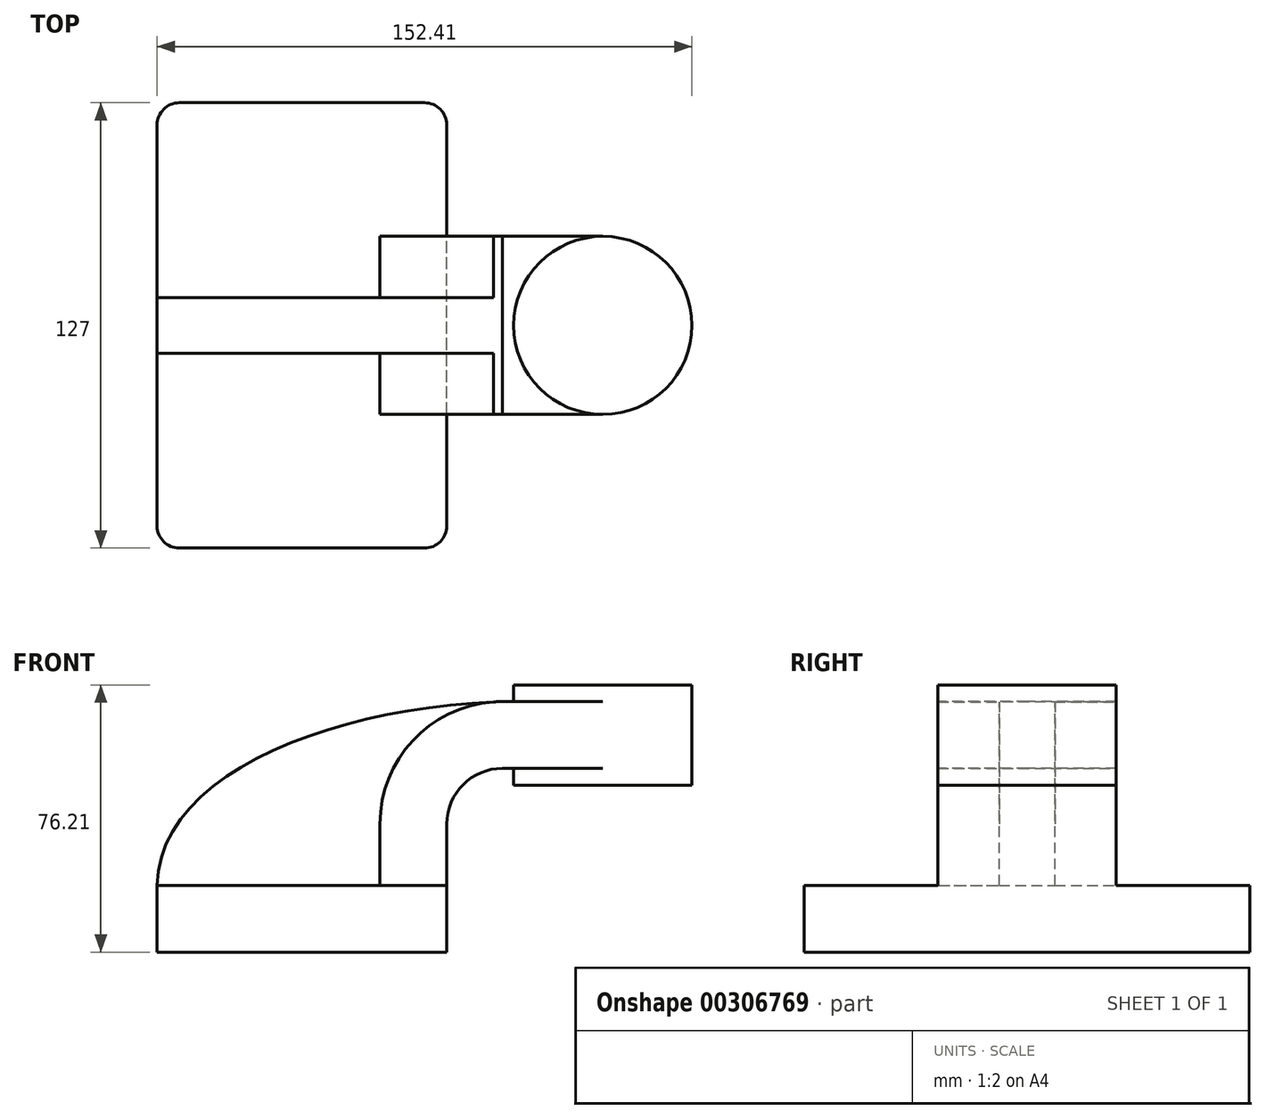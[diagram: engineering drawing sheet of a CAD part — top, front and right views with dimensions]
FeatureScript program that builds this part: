
annotation { "Feature Type Name" : "Feature", "Feature Type Description" : "" }
export const myFeature = defineFeature(function(context is Context, id is Id, definition is map)
    precondition{}
    {
        {
            var Q0;
            Q0=qCreatedBy(makeId("Front.planeOp"),FACE);
            var sketch = newSketch(context, id + "F0", { "sketchPlane" : qUnion([Q0])});
            skLineSegment(sketch, "E0.bottom", {"start": v(41.28, -9.52) * mm, "end": v(-41.28, -9.53) * mm});
            skLineSegment(sketch, "E0.top", {"start": v(41.27, 9.53) * mm, "end": v(-41.28, 9.53) * mm});
            skLineSegment(sketch, "E0.left", {"start": v(41.28, -9.52) * mm, "end": v(41.28, 9.53) * mm});
            skLineSegment(sketch, "E0.right", {"start": v(-41.28, -9.53) * mm, "end": v(-41.28, 9.53) * mm});
            skPoint(sketch, "E0.middle", {"position": v(0, 0) * mm});
            skLineSegment(sketch, "E1.bottom", {"start": v(111.12, 38.1) * mm, "end": v(60.33, 38.1) * mm});
            skLineSegment(sketch, "E1.top", {"start": v(111.12, 66.68) * mm, "end": v(60.33, 66.68) * mm});
            skLineSegment(sketch, "E1.left", {"start": v(111.12, 38.1) * mm, "end": v(111.12, 66.68) * mm});
            skLineSegment(sketch, "E1.right", {"start": v(60.33, 38.1) * mm, "end": v(60.33, 66.68) * mm});
            skPoint(sketch, "E1.middle", {"position": v(85.72, 52.39) * mm});
            skLineSegment(sketch, "E2", {"start": v(41.27, 9.53) * mm, "end": v(41.27, 27) * mm});
            skArc(sketch, "E3", {"start": v(41.27, 27) * mm, "mid": v(45.92, 38.23) * mm, "end": v(57.15, 42.88) * mm});
            skLineSegment(sketch, "E4", {"start": v(57.15, 42.88) * mm, "end": v(85.72, 42.88) * mm});
            skLineSegment(sketch, "E5", {"start": v(85.72, 42.88) * mm, "end": v(85.72, 42.88) * mm});
            skLineSegment(sketch, "E6.0", {"start": v(57.15, 61.93) * mm, "end": v(85.72, 61.93) * mm});
            skArc(sketch, "E6.1", {"start": v(22.23, 27) * mm, "mid": v(32.45, 51.7) * mm, "end": v(57.15, 61.93) * mm});
            skLineSegment(sketch, "E6.2", {"start": v(22.22, 9.53) * mm, "end": v(22.22, 27) * mm});
            skLineSegment(sketch, "E7", {"start": v(85.72, 38.1) * mm, "end": v(85.72, 66.68) * mm});
            skFitSpline(sketch, "E8", {"points": [v(-41.28, 9.53) * mm, v(57.15, 61.93) * mm], "startDerivative": vector(1.72, 97.18) * mm, "endDerivative": vector(142.4, 4.43) * mm});
            skSolve(sketch);
        }
        {
            var Q0;
            Q0=makeQuery(id+"F0.imprint","IMPRINT",FACE,{"disambiguationData":[TD([[makeQuery(id+"F0.imprint","IMPRINT",EDGE,{"derivedFrom":sQuery(id+"F0.wireOp",EDGE,"E0.bottom")}),-1.0]])]});
            extrude(context, id + "F1", {"entities" : qUnion([Q0]), "endBound" : BoundingType.SYMMETRIC, "depth" : 127 * mm});
        }
        {
            var Q0;
            {var subQ1=sQuery(id+"F0.wireOp",EDGE,"E2");Q0=makeQuery(id+"F0.imprint","IMPRINT",FACE,{"disambiguationData":[TD([[makeQuery(id+"F0.imprint","IMPRINT",EDGE,{"derivedFrom":subQ1}),1.0]])]});}
            var Q1;
            {var subQ0=sQuery(id+"F0.wireOp",EDGE,"E4");var subQ1=sQuery(id+"F0.wireOp",EDGE,"E1.right");var subQ2=makeQuery(id+"F0.imprint","INTERSECT",VERTEX,{"derivedFrom":[subQ1,subQ0]});Q1=makeQuery(id+"F0.imprint","IMPRINT",FACE,{"disambiguationData":[TD([[makeQuery(id+"F0.imprint","IMPRINT",EDGE,{"disambiguationData":[TD([[subQ2,-1.0]])],"derivedFrom":subQ1}),-1.0]])]});}
            extrude(context, id + "F2", {"entities" : qUnion([Q0, Q1]), "operationType" : NewBodyOperationType.ADD, "endBound" : BoundingType.SYMMETRIC, "depth" : 50.8 * mm});
        }
        {
            var Q0;
            {var subQ3=sQuery(id+"F0.wireOp",EDGE,"E6.2");Q0=makeQuery(id+"F0.imprint","IMPRINT",FACE,{"disambiguationData":[TD([[makeQuery(id+"F0.imprint","IMPRINT",EDGE,{"derivedFrom":subQ3}),1.0]])]});}
            extrude(context, id + "F3", {"entities" : qUnion([Q0]), "operationType" : NewBodyOperationType.ADD, "endBound" : BoundingType.SYMMETRIC, "depth" : 15.88 * mm});
        }
        {
            var Q0;
            {var subQ0=sQuery(id+"F0.wireOp",EDGE,"E1.left");Q0=makeQuery(id+"F0.imprint","IMPRINT",FACE,{"disambiguationData":[TD([[makeQuery(id+"F0.imprint","IMPRINT",EDGE,{"derivedFrom":subQ0}),1.0]])]});}
            var Q1;
            Q1=sQuery(id+"F0.wireOp",EDGE,"E7");
            revolve(context, id + "F4", {"operationType" : NewBodyOperationType.ADD, "entities" : qUnion([Q0]), "axis" : qUnion([Q1]), "revolveType" : RevolveType.FULL});
        }
        {
            var Q0;
            Q0=makeQuery(id+"F1.opExtrude","CAP_EDGE",EDGE,{"disambiguationData":[OSD([sQuery(id+"F0.wireOp",EDGE,"E0.left")])],"isStart":false});
            var Q1;
            Q1=makeQuery(id+"F1.opExtrude","CAP_EDGE",EDGE,{"disambiguationData":[OSD([sQuery(id+"F0.wireOp",EDGE,"E0.right")])],"isStart":false});
            var Q2;
            Q2=makeQuery(id+"F1.opExtrude","CAP_EDGE",EDGE,{"disambiguationData":[OSD([sQuery(id+"F0.wireOp",EDGE,"E0.left")])],"isStart":true});
            var Q3;
            Q3=makeQuery(id+"F1.opExtrude","CAP_EDGE",EDGE,{"disambiguationData":[OSD([sQuery(id+"F0.wireOp",EDGE,"E0.right")])],"isStart":true});
            fillet(context, id + "F5", {"entities" : qUnion([Q0, Q1, Q2, Q3]), "radius" : 6.35 * mm, "tangentPropagation" : true, "allowEdgeOverflow" : false});
        }
    });
